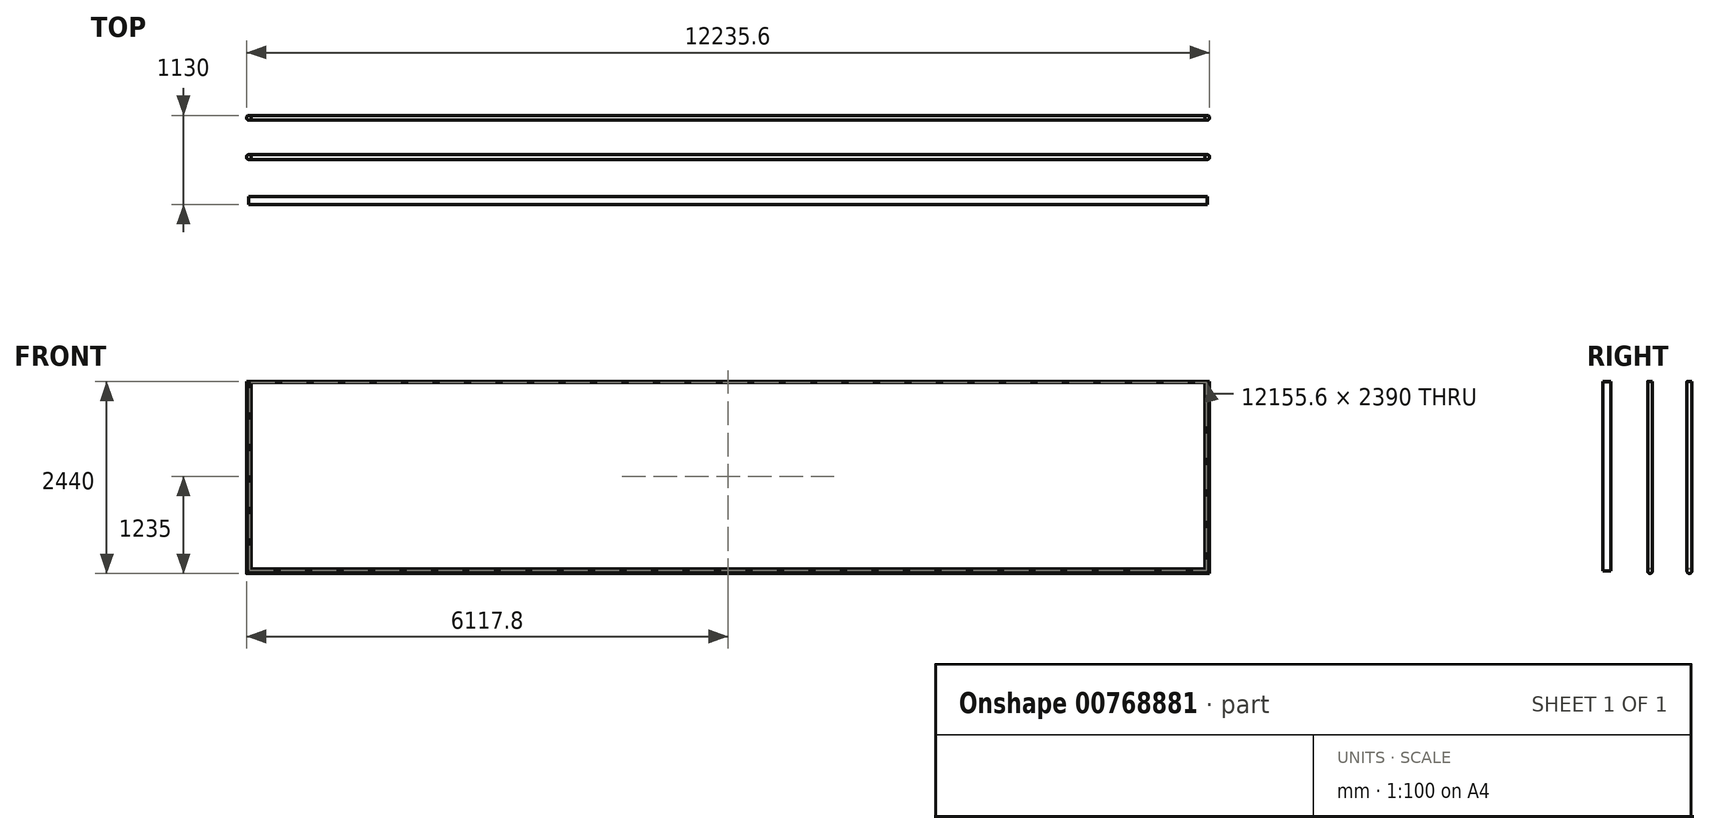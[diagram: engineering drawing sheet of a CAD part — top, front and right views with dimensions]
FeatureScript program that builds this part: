
annotation { "Feature Type Name" : "Feature", "Feature Type Description" : "" }
export const myFeature = defineFeature(function(context is Context, id is Id, definition is map)
    precondition{}
    {
        {
            var Q0;
            Q0=qCreatedBy(makeId("Front.planeOp"),FACE);
            var sketch = newSketch(context, id + "F0", { "sketchPlane" : qUnion([Q0])});
            skLineSegment(sketch, "E0.bottom", {"start": v(0, 0) * mm, "end": v(12175.6, 0) * mm});
            skLineSegment(sketch, "E0.top", {"start": v(0, 2410) * mm, "end": v(12175.6, 2410) * mm});
            skLineSegment(sketch, "E0.left", {"start": v(0, 0) * mm, "end": v(0, 2410) * mm});
            skLineSegment(sketch, "E0.right", {"start": v(12175.6, 0) * mm, "end": v(12175.6, 2410) * mm});
            skLineSegment(sketch, "E1.bottom", {"start": v(10, 10) * mm, "end": v(12165.6, 10) * mm});
            skLineSegment(sketch, "E1.top", {"start": v(10, 2400) * mm, "end": v(12165.6, 2400) * mm});
            skLineSegment(sketch, "E1.left", {"start": v(10, 10) * mm, "end": v(10, 2400) * mm});
            skLineSegment(sketch, "E1.right", {"start": v(12165.6, 10) * mm, "end": v(12165.6, 2400) * mm});
            skSolve(sketch);
        }
        {
            var Q0;
            Q0 = qSketchRegion(id + "F0", true);
            extrude(context, id + "F1", {"entities" : qUnion([Q0]), "depth" : 100 * mm, "offsetDistance" : 25 * mm});
        }
        {
            var Q0;
            Q0=qCreatedBy(makeId("Right.planeOp"),FACE);
            var sketch = newSketch(context, id + "F2", { "sketchPlane" : qUnion([Q0])});
            skCircle(sketch, "E2", {"center": v(1000, 0) * mm, "radius": 30 * mm});
            skCircle(sketch, "E3", {"center": v(500, 0) * mm, "radius": 30 * mm});
            skSolve(sketch);
        }
        {
            var Q0;
            Q0=qCreatedBy(makeId("Front.planeOp"),FACE);
            cPlane(context, id + "F3", {"entities" : qUnion([Q0]), "cplaneType" : CPlaneType.OFFSET, "offset" : 500 * mm, "oppositeDirection" : true, "width" : 150 * mm, "height" : 150 * mm});
        }
        {
            var Q0;
            Q0=qCreatedBy(id+"F3.planeOp",FACE);
            cPlane(context, id + "F4", {"entities" : qUnion([Q0]), "cplaneType" : CPlaneType.OFFSET, "offset" : 500 * mm, "oppositeDirection" : true, "width" : 150 * mm, "height" : 150 * mm});
        }
        {
            var Q0;
            Q0=qCreatedBy(id+"F3.planeOp",FACE);
            var sketch = newSketch(context, id + "F5", { "sketchPlane" : qUnion([Q0])});
            skLineSegment(sketch, "E4", {"start": v(0, 0) * mm, "end": v(12175.6, 0) * mm});
            skLineSegment(sketch, "E5", {"start": v(12175.6, 0) * mm, "end": v(12175.6, 2410) * mm});
            skLineSegment(sketch, "E6", {"start": v(12175.6, 2410) * mm, "end": v(0, 2410) * mm});
            skLineSegment(sketch, "E7", {"start": v(0, 2410) * mm, "end": v(0, 0) * mm});
            skSolve(sketch);
        }
        {
            var Q0;
            Q0=makeQuery(id+"F2.imprint","IMPRINT",FACE,{"disambiguationData":[TD([[makeQuery(id+"F2.imprint","IMPRINT",EDGE,{"derivedFrom":sQuery(id+"F2.wireOp",EDGE,"E3")}),1.0]])]});
            var Q1;
            Q1=sQuery(id+"F5.wireOp",EDGE,"E4");
            var Q2;
            Q2=sQuery(id+"F5.wireOp",EDGE,"E5");
            var Q3;
            Q3=sQuery(id+"F5.wireOp",EDGE,"E7");
            sweep(context, id + "F6", {"profiles" : qUnion([Q0]), "path" : qUnion([Q1, Q2, Q3])});
        }
        {
            var Q0;
            Q0=qCreatedBy(id+"F4.planeOp",FACE);
            var sketch = newSketch(context, id + "F7", { "sketchPlane" : qUnion([Q0])});
            skLineSegment(sketch, "E8.0", {"start": v(0, 0) * mm, "end": v(12175.6, 0) * mm});
            skLineSegment(sketch, "E9.0", {"start": v(12175.6, 0) * mm, "end": v(12175.6, 2410) * mm});
            skLineSegment(sketch, "E10.0", {"start": v(12175.6, 2410) * mm, "end": v(0, 2410) * mm});
            skLineSegment(sketch, "E11.0", {"start": v(0, 2410) * mm, "end": v(0, 0) * mm});
            skSolve(sketch);
        }
        {
            var Q0;
            Q0=makeQuery(id+"F2.imprint","IMPRINT",FACE,{"disambiguationData":[TD([[makeQuery(id+"F2.imprint","IMPRINT",EDGE,{"derivedFrom":sQuery(id+"F2.wireOp",EDGE,"E2")}),1.0]])]});
            var Q1;
            Q1=sQuery(id+"F7.wireOp",EDGE,"E8.0");
            var Q2;
            Q2=sQuery(id+"F7.wireOp",EDGE,"E9.0");
            var Q3;
            Q3=sQuery(id+"F7.wireOp",EDGE,"E11.0");
            sweep(context, id + "F8", {"profiles" : qUnion([Q0]), "path" : qUnion([Q1, Q2, Q3])});
        }
    });
